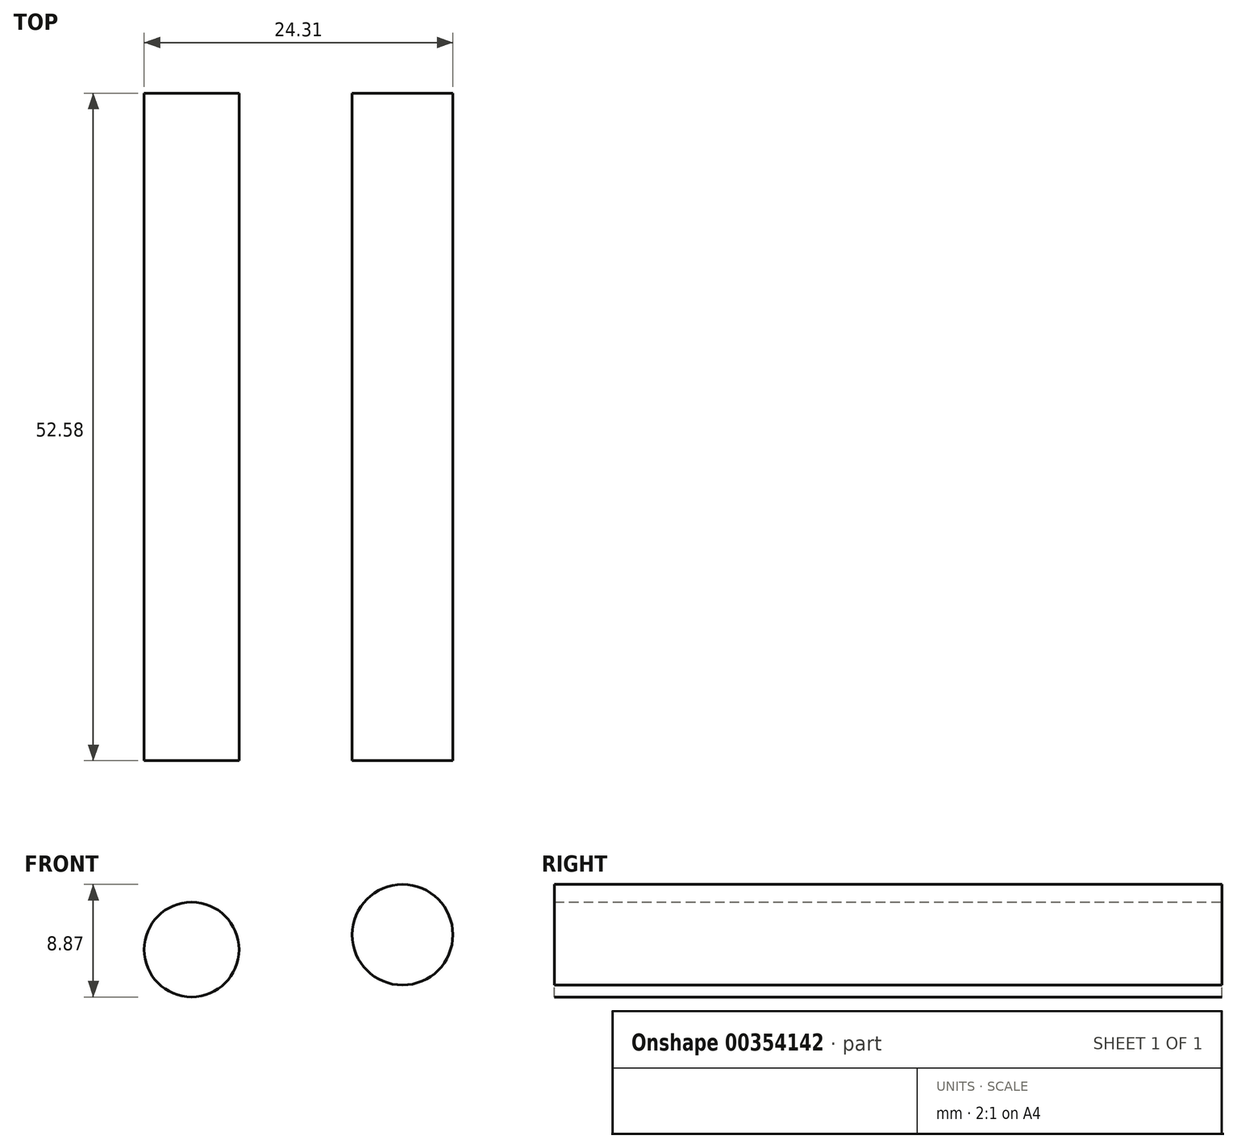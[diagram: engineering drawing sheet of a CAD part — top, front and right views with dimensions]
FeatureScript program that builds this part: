
annotation { "Feature Type Name" : "Feature", "Feature Type Description" : "" }
export const myFeature = defineFeature(function(context is Context, id is Id, definition is map)
    precondition{}
    {
        {
            var Q0;
            Q0=qCreatedBy(makeId("Front.planeOp"),FACE);
            var sketch = newSketch(context, id + "F0", { "sketchPlane" : qUnion([Q0])});
            skCircle(sketch, "E0", {"center": v(-38.77, 19.97) * mm, "radius": 3.73 * mm});
            skCircle(sketch, "E1", {"center": v(-22.15, 21.13) * mm, "radius": 3.96 * mm});
            skSolve(sketch);
        }
        {
            var Q0;
            Q0 = qSketchRegion(id + "F0", true);
            extrude(context, id + "F1", {"entities" : qUnion([Q0]), "depth" : 52.58 * mm});
        }
    });
